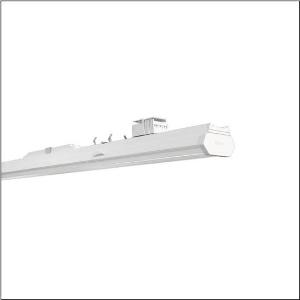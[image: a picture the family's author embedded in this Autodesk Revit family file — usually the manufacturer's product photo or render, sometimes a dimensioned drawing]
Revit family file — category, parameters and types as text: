
# Revit family: licross_21_protected_mo_52td1bmn4axg
name_source: partatom
category: Lighting Fixtures
units: mm (PartAtom-declared; Revit-internal decimal feet)

## family parameters
Cut with Voids When Loaded = No
Host = Face
Light Source = No
Part Type = Normal
Room Calculation Point = No
Round Connector Dimension = Use Diameter
Shared = No

## types (1)
- --- (1 x LED, 10100 lm, 60.5 W, 4000K)
    Apparent Load = 61 VA
    CIE Flux Codes = 54 82 95 97 100
    Color Rendering = 80
    Color Temperature = 4000K
    Default Elevation = 1800 mm
    Description = Licross 21 Protected MO, luminaire insert, of sheet steel, galvanised, coil coated, white, length: 1.500mm, width: 90mm, height: 103mm, LED rated luminous flux: 10.100lm, light colour: 840, SDCM (Standard Deviation of Colour Matching)MacAdam ≤ 3 SDCM (initial), control gear: ON/OFF Multilumen, with plug, 3-pole, with phase selection, mains connection: 220..240V, AC, 50/60Hz, rated input power: 61W, internal wiring halogen-free, primary optical cover: cover, of PMMA, light emission: direct distribution, primary light characteristic: symmetric, protection rating (complete): IP54, insulation class (complete): insulation class I (protective earthing), certification: CE, ENEC, VDE, UKCA, protection symbol: D if used in an environment with non-conductive dust loads with corresponding accessories, impact resistance: IK06, permissible ambient temperature for indoor applications: -35..+45°C, corresponds to IFS (International Featured Standards) requirements for safety and quality in the food industry, reducing of maximum allowable ambient temperature of 5°C with ceiling mounting, LABS conformity tested according to VDMA 24364:2018-05, The light source and the operating device comply with the requirements of the Ecodesign Regulation (EU) 2019/2020 and are replaceable in accordance with this regulation, packaging unit: 1 piece
    Height = 92 mm
    Lamp = 1 x LED
    Lamp Light Flux = 10100 lm
    Lamp Power = 60.5 W
    Lamp count = 1
    Length = 1500 mm
    Luminous efficacy = 167 lm/W
    Manufacturer = Siteco
    ModVariant = No
    Model = 52TD1BMN4AXG
    Mounting Place = Ceiling
    Mounting Type = Pendant
    Number of Poles = 1
    OnlyDefault = Yes
    Power Factor = 1
    Product Name = Licross 21 Protected MO
    Product group = luminaire insert | ceiling pendant
    ProductGroupID = 901
    Protection Class = Protection class I
    Protection Degree = IP 54
    RLX_Detail_Level = 1
    RLX_Emergency_Light_Flux = 0 lm
    RLX_Emergency_Type = 0
    RLX_Emergency_Type_DB = No
    RlxData = <blob elided: 22305 chars, md5=b8992db0>
    Socket = socket
    Standby Power = 0 W
    System Light Flux = 10100 lm
    System Power = 61 W
    Type Comments = factory setting: luminous flux: 100 % | (A | C | E) | 140 mA
    Type Image = l_1256148.jpg
    URL = http://relux.com
    VarID = @adj_110693
    Voltage = 0 V
    Weight = 0.00 kg
    Width = 88 mm

## geometry (parser evidence)
native form markers: Blend x4, Sweep x10
no freeform markers — native parametric forms only
